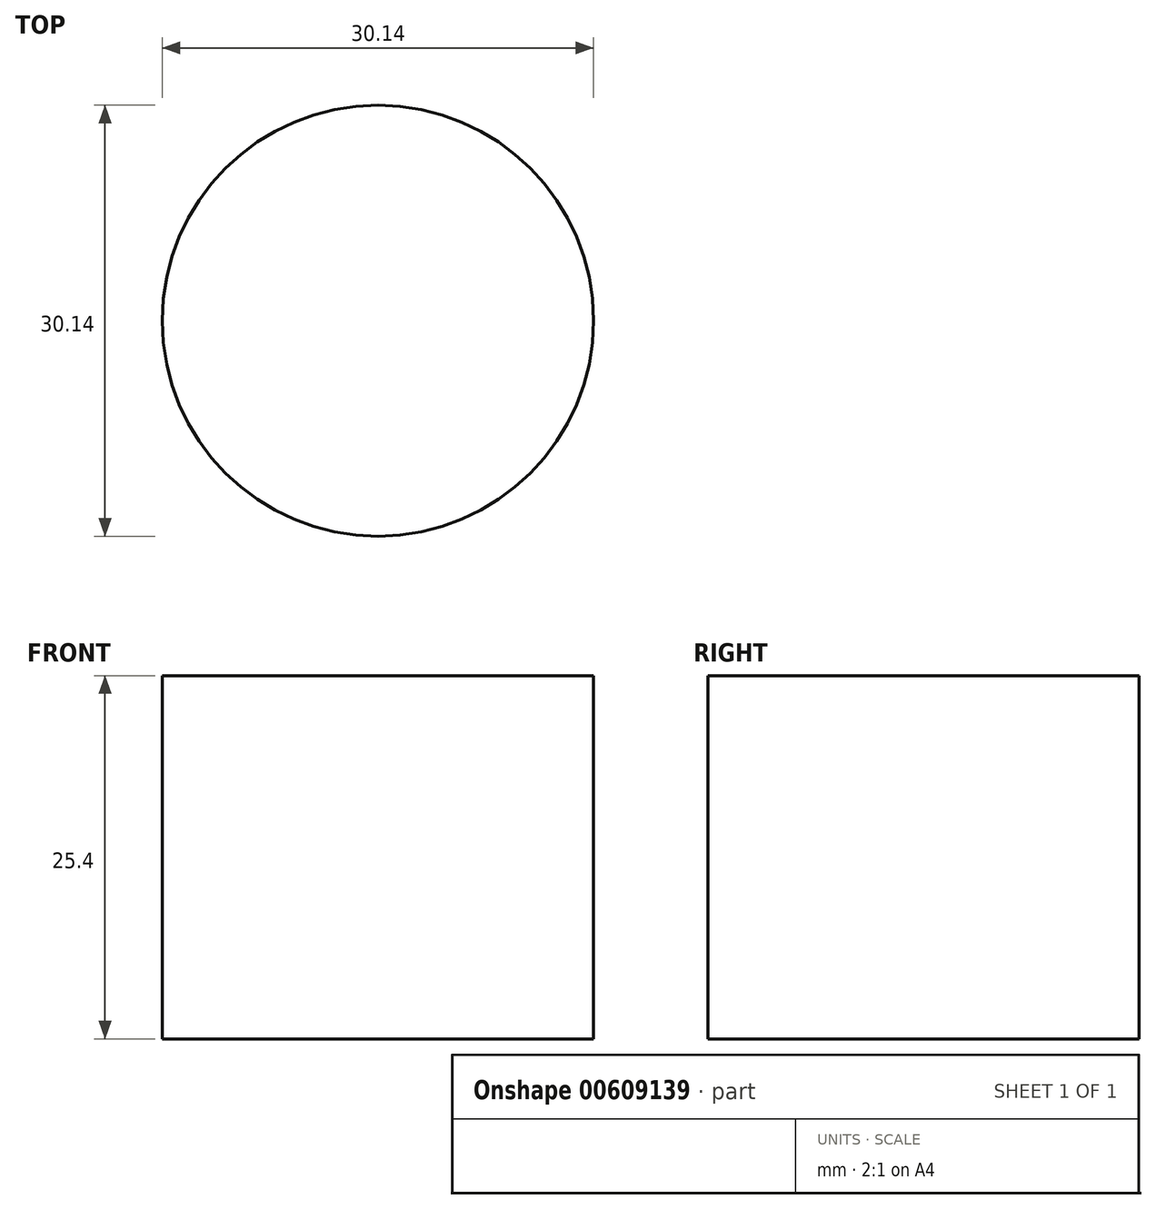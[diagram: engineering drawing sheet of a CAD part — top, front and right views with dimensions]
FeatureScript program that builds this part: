
annotation { "Feature Type Name" : "Feature", "Feature Type Description" : "" }
export const myFeature = defineFeature(function(context is Context, id is Id, definition is map)
    precondition{}
    {
        {
            var Q0;
            Q0=qCreatedBy(makeId("Top.planeOp"),FACE);
            var sketch = newSketch(context, id + "F0", { "sketchPlane" : qUnion([Q0])});
            skLineSegment(sketch, "E0.bottom", {"start": v(-84.71, 44.15) * mm, "end": v(87.1, 44.15) * mm});
            skLineSegment(sketch, "E0.top", {"start": v(-84.71, -43.42) * mm, "end": v(87.1, -43.42) * mm});
            skLineSegment(sketch, "E0.left", {"start": v(-84.71, 44.15) * mm, "end": v(-84.71, -43.42) * mm});
            skLineSegment(sketch, "E0.right", {"start": v(87.1, 44.15) * mm, "end": v(87.1, -43.42) * mm});
            skCircle(sketch, "E1", {"center": v(0, 28.67) * mm, "radius": 15.07 * mm});
            skCircle(sketch, "E2", {"center": v(-68.43, 5.1) * mm, "radius": 4.1 * mm});
            skCircle(sketch, "E3", {"center": v(-50.85, 5.3) * mm, "radius": 4.57 * mm});
            skCircle(sketch, "E4", {"center": v(-76.38, -7.84) * mm, "radius": 3.67 * mm});
            skCircle(sketch, "E5", {"center": v(-76.2, -20.6) * mm, "radius": 3.72 * mm});
            skCircle(sketch, "E6", {"center": v(-43.09, -7.47) * mm, "radius": 4.22 * mm});
            skCircle(sketch, "E7", {"center": v(-42.53, -21.34) * mm, "radius": 3.71 * mm});
            skCircle(sketch, "E8", {"center": v(-67.32, -35.96) * mm, "radius": 4.84 * mm});
            skCircle(sketch, "E9", {"center": v(-50.48, -35.96) * mm, "radius": 4.7 * mm});
            skCircle(sketch, "E10", {"center": v(51.43, 33.4) * mm, "radius": 4.38 * mm});
            skCircle(sketch, "E11", {"center": v(70.11, 31.74) * mm, "radius": 5.63 * mm});
            skCircle(sketch, "E12", {"center": v(55.87, -5.07) * mm, "radius": 3.46 * mm});
            skCircle(sketch, "E13", {"center": v(76.03, -8.77) * mm, "radius": 6.02 * mm});
            skSolve(sketch);
        }
        {
            var Q0;
            Q0=makeQuery(id+"F0.imprint","IMPRINT",FACE,{"disambiguationData":[TD([[makeQuery(id+"F0.imprint","IMPRINT",EDGE,{"derivedFrom":sQuery(id+"F0.wireOp",EDGE,"E1")}),1.0]])]});
            extrude(context, id + "F1", {"entities" : qUnion([Q0]), "depth" : 25.4 * mm, "offsetDistance" : 25.4 * mm});
        }
    });
